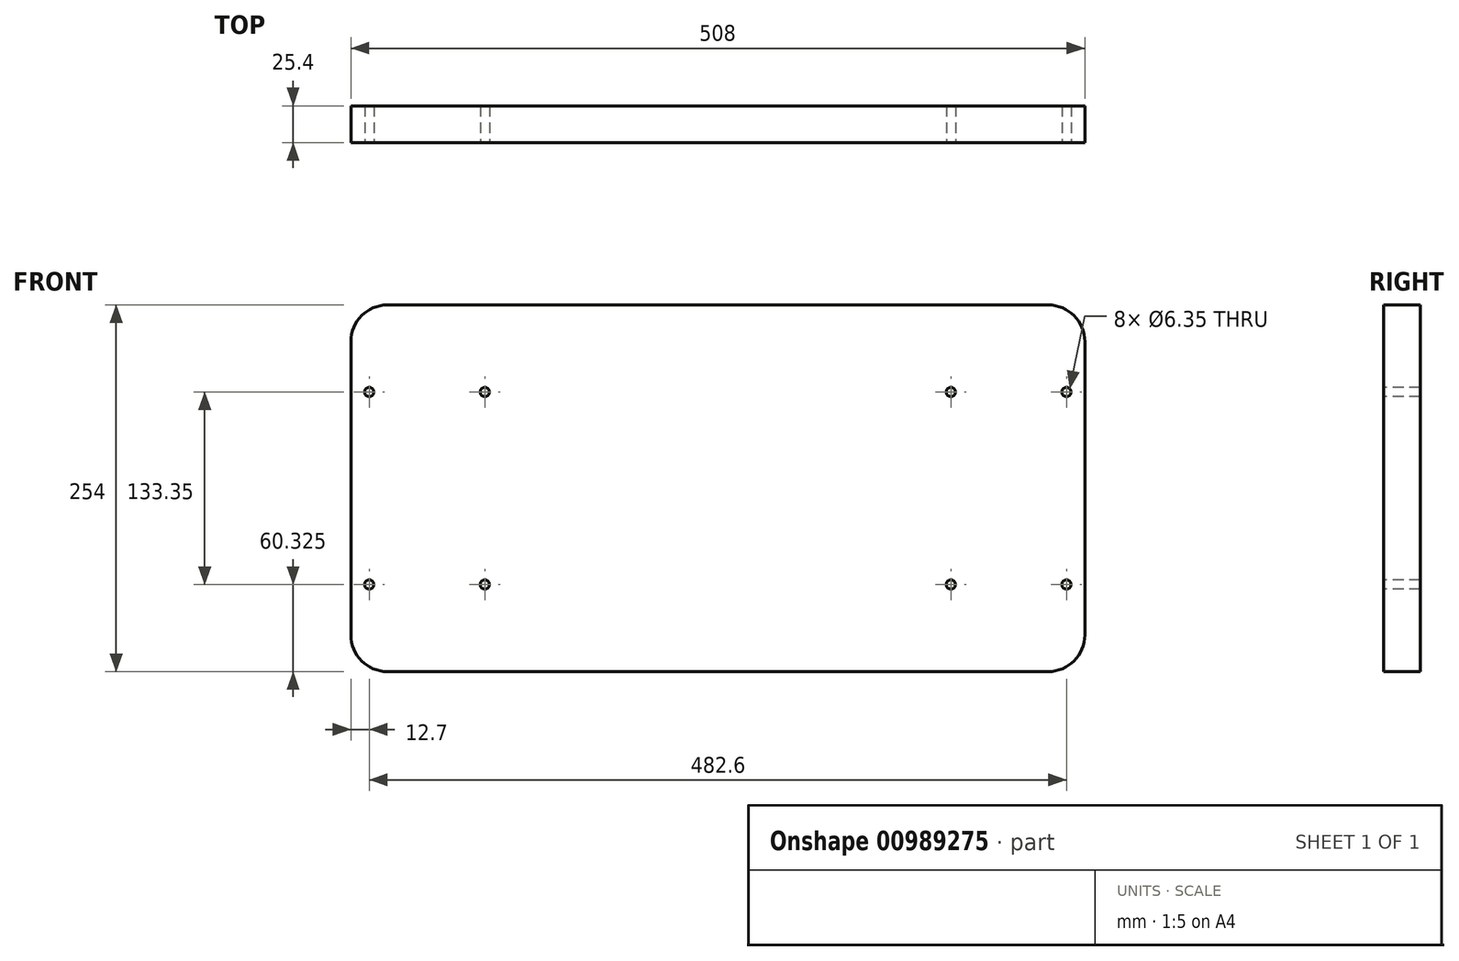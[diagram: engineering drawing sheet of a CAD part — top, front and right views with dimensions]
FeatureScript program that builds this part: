
annotation { "Feature Type Name" : "Feature", "Feature Type Description" : "" }
export const myFeature = defineFeature(function(context is Context, id is Id, definition is map)
    precondition{}
    {
        {
            var Q0;
            Q0=qCreatedBy(makeId("Front.planeOp"),FACE);
            var sketch = newSketch(context, id + "F0", { "sketchPlane" : qUnion([Q0])});
            skLineSegment(sketch, "E0", {"start": v(0, 25.4) * mm, "end": v(0, 228.6) * mm});
            skLineSegment(sketch, "E1", {"start": v(25.4, 254) * mm, "end": v(482.6, 254) * mm});
            skLineSegment(sketch, "E2", {"start": v(508, 228.6) * mm, "end": v(508, 25.4) * mm});
            skLineSegment(sketch, "E3", {"start": v(482.6, 0) * mm, "end": v(25.4, 0) * mm});
            skPoint(sketch, "E4.visualSharp", {"position": v(0, 254) * mm});
            skArc(sketch, "E4.filletArc", {"start": v(25.4, 254) * mm, "mid": v(7.44, 246.56) * mm, "end": v(0, 228.6) * mm});
            skPoint(sketch, "E5.visualSharp", {"position": v(508, 254) * mm});
            skArc(sketch, "E5.filletArc", {"start": v(508, 228.6) * mm, "mid": v(500.56, 246.56) * mm, "end": v(482.6, 254) * mm});
            skPoint(sketch, "E6.visualSharp", {"position": v(508, 0) * mm});
            skArc(sketch, "E6.filletArc", {"start": v(482.6, 0) * mm, "mid": v(500.56, 7.44) * mm, "end": v(508, 25.4) * mm});
            skPoint(sketch, "E7.visualSharp", {"position": v(0, 0) * mm});
            skArc(sketch, "E7.filletArc", {"start": v(0, 25.4) * mm, "mid": v(7.44, 7.44) * mm, "end": v(25.4, 0) * mm});
            skSolve(sketch);
        }
        {
            var Q0;
            Q0 = qSketchRegion(id + "F0", true);
            extrude(context, id + "F1", {"entities" : qUnion([Q0]), "depth" : 25.4 * mm, "offsetDistance" : 25.4 * mm});
        }
        {
            var Q0;
            Q0=makeQuery(id+"F1.opExtrude","CAP_FACE",FACE,{"disambiguationData":[OSD([sQuery(id+"F0.wireOp",EDGE,"E0"),sQuery(id+"F0.wireOp",EDGE,"E1"),sQuery(id+"F0.wireOp",EDGE,"E2"),sQuery(id+"F0.wireOp",EDGE,"E3"),sQuery(id+"F0.wireOp",EDGE,"E4.filletArc"),sQuery(id+"F0.wireOp",EDGE,"E5.filletArc"),sQuery(id+"F0.wireOp",EDGE,"E6.filletArc"),sQuery(id+"F0.wireOp",EDGE,"E7.filletArc")])],"isStart":false});
            var sketch = newSketch(context, id + "F2", { "sketchPlane" : qUnion([Q0])});
            skPoint(sketch, "E8", {"position": v(12.7, 193.67) * mm});
            skLineSegment(sketch, "E9", {"start": v(254, 254) * mm, "end": v(254, 0) * mm, "construction": true});
            skLineSegment(sketch, "E10", {"start": v(0, 127) * mm, "end": v(508, 127) * mm, "construction": true});
            skPoint(sketch, "E11", {"position": v(92.71, 193.67) * mm});
            skPoint(sketch, "E12.MirrorP", {"position": v(415.3, 193.67) * mm});
            skPoint(sketch, "E13.MirrorP", {"position": v(495.3, 193.67) * mm});
            skPoint(sketch, "E14.MirrorP", {"position": v(92.71, 60.33) * mm});
            skPoint(sketch, "E15.MirrorP", {"position": v(12.7, 60.33) * mm});
            skPoint(sketch, "E16.MirrorP", {"position": v(415.3, 60.33) * mm});
            skPoint(sketch, "E17.MirrorP", {"position": v(495.3, 60.33) * mm});
            skSolve(sketch);
        }
        {
            var Q0;
            Q0=sQuery(id+"F2.wireOp",VERTEX,"E8");
            var Q1;
            Q1=sQuery(id+"F2.wireOp",VERTEX,"E11");
            var Q2;
            Q2=sQuery(id+"F2.wireOp",VERTEX,"E15.MirrorP");
            var Q3;
            Q3=sQuery(id+"F2.wireOp",VERTEX,"E14.MirrorP");
            var Q4;
            Q4=sQuery(id+"F2.wireOp",VERTEX,"E12.MirrorP");
            var Q5;
            Q5=sQuery(id+"F2.wireOp",VERTEX,"E13.MirrorP");
            var Q6;
            Q6=sQuery(id+"F2.wireOp",VERTEX,"E16.MirrorP");
            var Q7;
            Q7=sQuery(id+"F2.wireOp",VERTEX,"E17.MirrorP");
            var Q8;
            Q8=makeQuery(id+"F1.opExtrude","SWEPT_BODY",BODY,{"disambiguationData":[OSD([sQuery(id+"F0.wireOp",EDGE,"E0"),sQuery(id+"F0.wireOp",EDGE,"E1"),sQuery(id+"F0.wireOp",EDGE,"E2"),sQuery(id+"F0.wireOp",EDGE,"E3"),sQuery(id+"F0.wireOp",EDGE,"E4.filletArc"),sQuery(id+"F0.wireOp",EDGE,"E5.filletArc"),sQuery(id+"F0.wireOp",EDGE,"E6.filletArc"),sQuery(id+"F0.wireOp",EDGE,"E7.filletArc")])]});
            hole(context, id + "F3", {"style" : HoleStyle.SIMPLE, "endStyle" : HoleEndStyle.THROUGH, "holeDiameter" : 6.35 * mm, "majorDiameter" : 6.35 * mm, "isTappedThrough" : true, "tappedDepth" : 12.7 * mm, "tapClearance" : 3, "locations" : qUnion([Q0, Q1, Q2, Q3, Q4, Q5, Q6, Q7]), "scope" : qUnion([Q8])});
        }
    });
